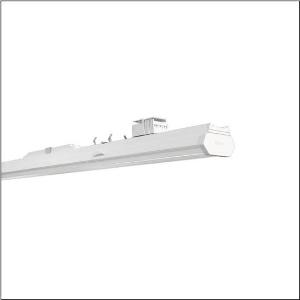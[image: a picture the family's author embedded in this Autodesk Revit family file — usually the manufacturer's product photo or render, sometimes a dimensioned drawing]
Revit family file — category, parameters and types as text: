
# Revit family: licross_r__11_protected_ho_51tp12dn5exl_83db
name_source: partatom
category: Lighting Fixtures
units: mm (PartAtom-declared; Revit-internal decimal feet)

## family parameters
Cut with Voids When Loaded = No
Host = Face
Light Source = No
Part Type = Normal
Room Calculation Point = No
Round Connector Dimension = Use Diameter
Shared = No

## types (1)
- --- (1 x LED, 14100 lm, 86.1 W, 5000K)
    Apparent Load = 86 VA
    CIE Flux Codes = 70 91 97 98 100
    Color Rendering = 80
    Color Temperature = 5000K
    Default Elevation = 1800 mm
    Description = Licross® 11 Protected HO, luminaire insert, of sheet steel, galvanised, coil coated, white, length: 1.500mm, width: 90mm, height: 101mm, LED rated luminous flux: 14.100lm, light colour: 850, control gear: DALI 2, control gear: ECG DALI, with plug, 5-pole, with phase selection, mains connection: 220..240V, AC, 50/60Hz, rated input power: 86W, halogen-free wiring, primary optical cover: cover, of PMMA, light emission: direct distribution, primary light characteristic: symmetric, protection rating (complete): IP64, insulation class (complete): insulation class I (protective earthing), certification: CE, ENEC, VDE, UKCA, protection symbol: D if used in an environment with conductive dust loads with corresponding accessories, impact resistance: IK06, permissible ambient temperature for indoor applications: -25..+35°C, reducing of maximum allowable ambient temperature of 5°C with ceiling mounting, corresponds to IFS (International Featured Standards) requirements for safety and quality in the food industry, LABS conformity tested according to VDMA 24364:2018-05, packaging unit: 1 piece
    Height = 92 mm
    Lamp = 1 x LED
    Lamp Light Flux = 14100 lm
    Lamp Power = 86.1 W
    Lamp count = 1
    Length = 1500 mm
    Luminous efficacy = 164 lm/W
    Manufacturer = Siteco
    ModVariant = No
    Model = 51TP12DN5EXL
    Mounting Place = Ceiling
    Mounting Type = Pendant
    Number of Poles = 1
    OnlyDefault = Yes
    Power Factor = 1
    Product Name = Licross® 11 Protected HO
    Product group = luminaire insert
    ProductGroupID = 901
    Protection Class = Protection class I
    Protection Degree = IP 64
    RLX_Detail_Level = 1
    RLX_Emergency_Light_Flux = 0 lm
    RLX_Emergency_Type = 0
    RLX_Emergency_Type_DB = No
    RlxData = <blob elided: 24165 chars, md5=92c08d4d>
    Socket = socket
    Standby Power = 0 W
    System Light Flux = 14100 lm
    System Power = 86 W
    Type Comments = factory setting: luminous flux: 100 % | dim-lin: 254 | 485 mA
    Type Image = l_1256148.jpg
    URL = http://relux.com
    VarID = @adj_158385
    Voltage = 0 V
    Weight = 0.00 kg
    Width = 88 mm

## geometry (parser evidence)
native form markers: Blend x4, Sweep x9
no freeform markers — native parametric forms only
